# Revit family: DC_Holyoake_OutsideLouver_OHL-F-45_supply_13
name_source: partatom
category: Air Terminals
revit_build: Autodesk Revit 2014 (Build: 20130308_1515(x64)
units: mm (PartAtom-declared; Revit-internal decimal feet)

## types (1)
- OHL-F-45
    Accessories = Aluminium Bird mesh or insect mesh (fibreglass)
    Blade Array Count = 9.948
    Blade Count = 9
    Blade Cut Setout = 450 mm  [stored 1.47638 ft]
    Blade Height = 61.6 mm  [stored 0.2021 ft]
    Blade Length = 397.4 mm  [stored 1.30381 ft]
    Blade Offset = 3.45 mm
    Blade Pitch = 50 mm  [stored 0.164042 ft]
    Blade Width = 44.8 mm  [stored 0.146982 ft]
    Description = Weather Louvres shall be Holyoake Model OHL-F-45 curved profile 45mm louvred blades set at 50mm centres and constructed in a 25mm flanged (F) frame to suit the installation profile.  Weather Louvres shall be of extruded aluminium construction and finished in natural anodised or powdercoat and fitted with accessories and dampers where indicated as manufactured by Holyoake.
    Exact Neck Height = 500 mm  [stored 1.64042 ft]
    Exact Neck Width = 400 mm  [stored 1.31234 ft]
    Exact Overall Flange Height = 548.2 mm
    Exact Overall Flange Width = 448.2 mm
    Flange Thickness = 4.7 mm
    Flange Width = 25.4 mm  [stored 0.0833333 ft]
    Holyoake Product Range = Outside Louvres
    Louver Depth = 51.7 mm  [stored 0.169619 ft]
    Manufacturer = Holyoake
    Material - Body = Holyoake Aluminium
    Material - Face = Holyoake Aluminium
    Max Flow = 2000.0 L/s
    Min Flow = 100.0 L/s
    Model = OHL-F-45
    Noise Level NC Max = 0.00 NC
    Noise Level NC Min = 0.00 NC
    Nominal Height = 506 mm
    Nominal Width = 406 mm  [stored 1.33202 ft]
    Overall Opening = 497.4 mm
    Static Pressure Max = 0.0 Pa
    Static Pressure Min = 0.0 Pa
    Top Blade Height = 47.4 mm
    Type Comments = 45mm Horizontal Curved Profile Louvers in Flanged Surround
    URL = http://www.holyoake.com

note: [stored X ft] marks values corroborated as IEEE doubles in the binary element streams (Revit-internal decimal feet)

## geometry (parser evidence)
native form markers: Blend x10, Sweep x8
no freeform markers — native parametric forms only
